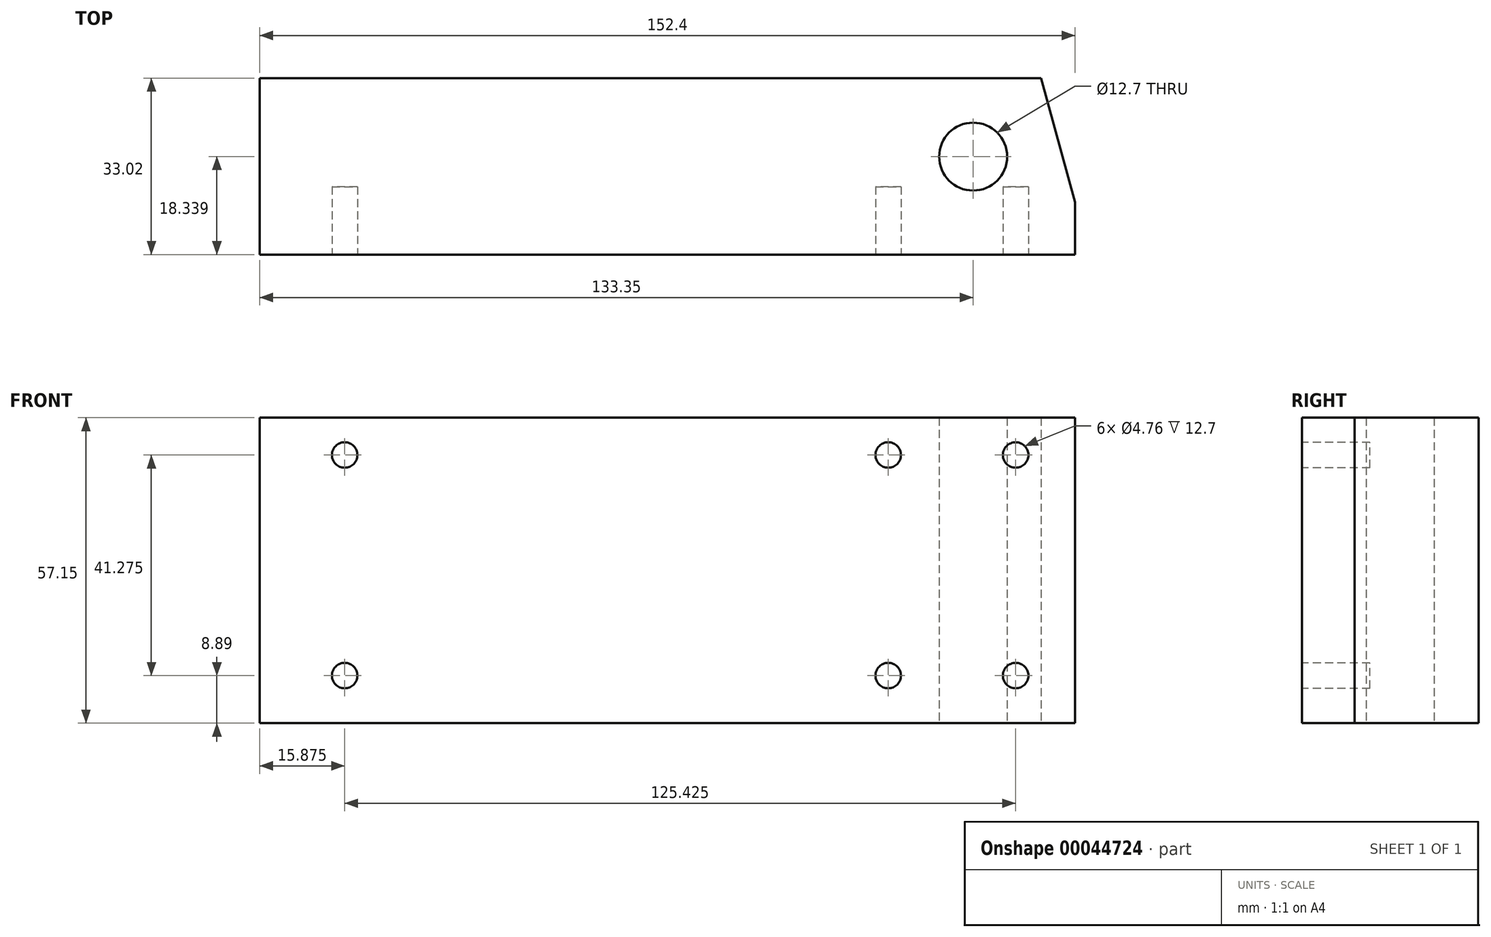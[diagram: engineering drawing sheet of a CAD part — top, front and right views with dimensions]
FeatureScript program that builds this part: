
annotation { "Feature Type Name" : "Feature", "Feature Type Description" : "" }
export const myFeature = defineFeature(function(context is Context, id is Id, definition is map)
    precondition{}
    {
        {
            var Q0;
            Q0=qCreatedBy(makeId("Top.planeOp"),FACE);
            var sketch = newSketch(context, id + "F0", { "sketchPlane" : qUnion([Q0])});
            skLineSegment(sketch, "E0", {"start": v(0, 0) * mm, "end": v(152.4, 0) * mm});
            skLineSegment(sketch, "E1", {"start": v(152.4, 0) * mm, "end": v(152.4, 33.02) * mm});
            skLineSegment(sketch, "E2", {"start": v(152.4, 33.02) * mm, "end": v(0, 33.02) * mm});
            skLineSegment(sketch, "E3", {"start": v(0, 33.02) * mm, "end": v(0, 0) * mm});
            skLineSegment(sketch, "E4", {"start": v(152.4, 18.34) * mm, "end": v(133.35, 18.34) * mm, "construction": true});
            skLineSegment(sketch, "E5", {"start": v(133.35, 18.34) * mm, "end": v(133.35, 33.02) * mm, "construction": true});
            skCircle(sketch, "E6", {"center": v(133.35, 18.34) * mm, "radius": 6.35 * mm});
            skLineSegment(sketch, "E7", {"start": v(152.4, 33.02) * mm, "end": v(146.05, 33.02) * mm, "construction": true});
            skLineSegment(sketch, "E8", {"start": v(152.4, 0) * mm, "end": v(152.4, 9.84) * mm});
            skLineSegment(sketch, "E9", {"start": v(152.4, 9.84) * mm, "end": v(146.05, 33.02) * mm});
            skSolve(sketch);
        }
        {
            var Q0;
            Q0=makeQuery(id+"F0.imprint","IMPRINT",FACE,{"disambiguationData":[TD([[makeQuery(id+"F0.imprint","IMPRINT",EDGE,{"derivedFrom":sQuery(id+"F0.wireOp",EDGE,"E0")}),1.0]])]});
            extrude(context, id + "F1", {"entities" : qUnion([Q0]), "depth" : 57.15 * mm});
        }
        {
            var Q0;
            Q0=makeQuery(id+"F1.opExtrude","SWEPT_FACE",FACE,{"disambiguationData":[OSD([sQuery(id+"F0.wireOp",EDGE,"E0")])]});
            var sketch = newSketch(context, id + "F2", { "sketchPlane" : qUnion([Q0])});
            skCircle(sketch, "E10.MirrorC", {"center": v(117.47, 50.16) * mm, "radius": 2.38 * mm});
            skCircle(sketch, "E11.MirrorC", {"center": v(117.48, 8.89) * mm, "radius": 2.38 * mm});
            skCircle(sketch, "E12.MirrorC", {"center": v(15.88, 50.16) * mm, "radius": 2.38 * mm});
            skCircle(sketch, "E13.MirrorC", {"center": v(15.88, 8.89) * mm, "radius": 2.38 * mm});
            skCircle(sketch, "E14.MirrorC", {"center": v(141.3, 8.89) * mm, "radius": 2.38 * mm});
            skCircle(sketch, "E15.MirrorC", {"center": v(141.3, 50.16) * mm, "radius": 2.38 * mm});
            skLineSegment(sketch, "E16.MirrorCS", {"start": v(117.48, 8.89) * mm, "end": v(141.3, 8.89) * mm});
            skLineSegment(sketch, "E17.MirrorCS", {"start": v(92.08, 50.16) * mm, "end": v(117.47, 50.16) * mm});
            skLineSegment(sketch, "E18.MirrorCS", {"start": v(92.08, 0) * mm, "end": v(92.08, 8.89) * mm});
            skLineSegment(sketch, "E19.MirrorCS", {"start": v(92.08, 8.89) * mm, "end": v(92.08, 50.16) * mm});
            skLineSegment(sketch, "E20.MirrorCS", {"start": v(117.47, 50.16) * mm, "end": v(117.48, 8.89) * mm});
            skLineSegment(sketch, "E21.MirrorCS", {"start": v(117.47, 50.16) * mm, "end": v(141.3, 50.16) * mm});
            skLineSegment(sketch, "E22.MirrorCS", {"start": v(141.3, 50.16) * mm, "end": v(141.3, 8.89) * mm});
            skLineSegment(sketch, "E23.MirrorCS", {"start": v(92.08, 8.89) * mm, "end": v(15.88, 8.89) * mm});
            skLineSegment(sketch, "E24.MirrorCS", {"start": v(92.08, 50.16) * mm, "end": v(15.88, 50.16) * mm});
            skLineSegment(sketch, "E25.MirrorCS", {"start": v(92.08, 8.89) * mm, "end": v(117.48, 8.89) * mm});
            skLineSegment(sketch, "E26.MirrorCS", {"start": v(15.88, 8.89) * mm, "end": v(15.88, 50.16) * mm});
            skLineSegment(sketch, "E27", {"start": v(152.4, 0) * mm, "end": v(141.3, 0) * mm, "construction": true});
            skLineSegment(sketch, "E28", {"start": v(141.3, 0) * mm, "end": v(141.3, 8.9) * mm, "construction": true});
            skSolve(sketch);
        }
        {
            var Q0;
            {var subQ1=sQuery(id+"F2.wireOp",EDGE,"E14.MirrorC");var subQ3=sQuery(id+"F2.wireOp",EDGE,"E16.MirrorCS");var subQ5=makeQuery(id+"F2.imprint","INTERSECT",VERTEX,{"derivedFrom":[subQ1,subQ3]});Q0=makeQuery(id+"F2.imprint","IMPRINT",FACE,{"disambiguationData":[TD([[makeQuery(id+"F2.imprint","IMPRINT",EDGE,{"disambiguationData":[TD([[subQ5,-1.0]])],"derivedFrom":subQ1}),1.0]])]});}
            var Q1;
            {var subQ1=sQuery(id+"F2.wireOp",EDGE,"E14.MirrorC");var subQ3=sQuery(id+"F2.wireOp",EDGE,"E16.MirrorCS");var subQ5=makeQuery(id+"F2.imprint","INTERSECT",VERTEX,{"derivedFrom":[subQ1,subQ3]});Q1=makeQuery(id+"F2.imprint","IMPRINT",FACE,{"disambiguationData":[TD([[makeQuery(id+"F2.imprint","IMPRINT",EDGE,{"disambiguationData":[TD([[subQ5,1.0]])],"derivedFrom":subQ1}),1.0]])]});}
            var Q2;
            {var subQ1=sQuery(id+"F2.wireOp",EDGE,"E15.MirrorC");var subQ3=sQuery(id+"F2.wireOp",EDGE,"E21.MirrorCS");var subQ5=makeQuery(id+"F2.imprint","INTERSECT",VERTEX,{"derivedFrom":[subQ1,subQ3]});Q2=makeQuery(id+"F2.imprint","IMPRINT",FACE,{"disambiguationData":[TD([[makeQuery(id+"F2.imprint","IMPRINT",EDGE,{"disambiguationData":[TD([[subQ5,-1.0]])],"derivedFrom":subQ1}),1.0]])]});}
            var Q3;
            {var subQ1=sQuery(id+"F2.wireOp",EDGE,"E15.MirrorC");var subQ3=sQuery(id+"F2.wireOp",EDGE,"E21.MirrorCS");var subQ5=makeQuery(id+"F2.imprint","INTERSECT",VERTEX,{"derivedFrom":[subQ1,subQ3]});Q3=makeQuery(id+"F2.imprint","IMPRINT",FACE,{"disambiguationData":[TD([[makeQuery(id+"F2.imprint","IMPRINT",EDGE,{"disambiguationData":[TD([[subQ5,1.0]])],"derivedFrom":subQ1}),1.0]])]});}
            var Q4;
            {var subQ1=sQuery(id+"F2.wireOp",EDGE,"E11.MirrorC");var subQ3=sQuery(id+"F2.wireOp",EDGE,"E16.MirrorCS");var subQ5=makeQuery(id+"F2.imprint","INTERSECT",VERTEX,{"derivedFrom":[subQ1,subQ3]});Q4=makeQuery(id+"F2.imprint","IMPRINT",FACE,{"disambiguationData":[TD([[makeQuery(id+"F2.imprint","IMPRINT",EDGE,{"disambiguationData":[TD([[subQ5,-1.0]])],"derivedFrom":subQ1}),1.0]])]});}
            var Q5;
            {var subQ1=sQuery(id+"F2.wireOp",EDGE,"E11.MirrorC");var subQ3=sQuery(id+"F2.wireOp",EDGE,"E16.MirrorCS");var subQ5=makeQuery(id+"F2.imprint","INTERSECT",VERTEX,{"derivedFrom":[subQ1,subQ3]});Q5=makeQuery(id+"F2.imprint","IMPRINT",FACE,{"disambiguationData":[TD([[makeQuery(id+"F2.imprint","IMPRINT",EDGE,{"disambiguationData":[TD([[subQ5,1.0]])],"derivedFrom":subQ1}),1.0]])]});}
            var Q6;
            {var subQ0=sQuery(id+"F2.wireOp",EDGE,"E20.MirrorCS");var subQ1=sQuery(id+"F2.wireOp",EDGE,"E10.MirrorC");var subQ2=makeQuery(id+"F2.imprint","INTERSECT",VERTEX,{"derivedFrom":[subQ1,subQ0]});Q6=makeQuery(id+"F2.imprint","IMPRINT",FACE,{"disambiguationData":[TD([[makeQuery(id+"F2.imprint","IMPRINT",EDGE,{"disambiguationData":[TD([[subQ2,1.0]])],"derivedFrom":subQ1}),1.0]])]});}
            var Q7;
            {var subQ1=sQuery(id+"F2.wireOp",EDGE,"E10.MirrorC");var subQ3=sQuery(id+"F2.wireOp",EDGE,"E17.MirrorCS");var subQ5=makeQuery(id+"F2.imprint","INTERSECT",VERTEX,{"derivedFrom":[subQ1,subQ3]});Q7=makeQuery(id+"F2.imprint","IMPRINT",FACE,{"disambiguationData":[TD([[makeQuery(id+"F2.imprint","IMPRINT",EDGE,{"disambiguationData":[TD([[subQ5,1.0]])],"derivedFrom":subQ1}),1.0]])]});}
            var Q8;
            {var subQ1=sQuery(id+"F2.wireOp",EDGE,"E10.MirrorC");var subQ3=sQuery(id+"F2.wireOp",EDGE,"E20.MirrorCS");var subQ5=makeQuery(id+"F2.imprint","INTERSECT",VERTEX,{"derivedFrom":[subQ1,subQ3]});Q8=makeQuery(id+"F2.imprint","IMPRINT",FACE,{"disambiguationData":[TD([[makeQuery(id+"F2.imprint","IMPRINT",EDGE,{"disambiguationData":[TD([[subQ5,-1.0]])],"derivedFrom":subQ1}),1.0]])]});}
            var Q9;
            {var subQ1=sQuery(id+"F2.wireOp",EDGE,"E13.MirrorC");var subQ3=sQuery(id+"F2.wireOp",EDGE,"E23.MirrorCS");var subQ5=makeQuery(id+"F2.imprint","INTERSECT",VERTEX,{"derivedFrom":[subQ1,subQ3]});Q9=makeQuery(id+"F2.imprint","IMPRINT",FACE,{"disambiguationData":[TD([[makeQuery(id+"F2.imprint","IMPRINT",EDGE,{"disambiguationData":[TD([[subQ5,-1.0]])],"derivedFrom":subQ1}),1.0]])]});}
            var Q10;
            {var subQ1=sQuery(id+"F2.wireOp",EDGE,"E13.MirrorC");var subQ3=sQuery(id+"F2.wireOp",EDGE,"E23.MirrorCS");var subQ5=makeQuery(id+"F2.imprint","INTERSECT",VERTEX,{"derivedFrom":[subQ1,subQ3]});Q10=makeQuery(id+"F2.imprint","IMPRINT",FACE,{"disambiguationData":[TD([[makeQuery(id+"F2.imprint","IMPRINT",EDGE,{"disambiguationData":[TD([[subQ5,1.0]])],"derivedFrom":subQ1}),1.0]])]});}
            var Q11;
            {var subQ0=sQuery(id+"F2.wireOp",EDGE,"E24.MirrorCS");var subQ1=sQuery(id+"F2.wireOp",EDGE,"E12.MirrorC");var subQ2=makeQuery(id+"F2.imprint","INTERSECT",VERTEX,{"derivedFrom":[subQ1,subQ0]});Q11=makeQuery(id+"F2.imprint","IMPRINT",FACE,{"disambiguationData":[TD([[makeQuery(id+"F2.imprint","IMPRINT",EDGE,{"disambiguationData":[TD([[subQ2,1.0]])],"derivedFrom":subQ1}),1.0]])]});}
            var Q12;
            {var subQ0=sQuery(id+"F2.wireOp",EDGE,"E24.MirrorCS");var subQ1=sQuery(id+"F2.wireOp",EDGE,"E12.MirrorC");var subQ2=makeQuery(id+"F2.imprint","INTERSECT",VERTEX,{"derivedFrom":[subQ1,subQ0]});Q12=makeQuery(id+"F2.imprint","IMPRINT",FACE,{"disambiguationData":[TD([[makeQuery(id+"F2.imprint","IMPRINT",EDGE,{"disambiguationData":[TD([[subQ2,-1.0]])],"derivedFrom":subQ1}),1.0]])]});}
            var Q13;
            {var subQ0=sQuery(id+"F2.wireOp",EDGE,"E25.MirrorCS");var subQ1=sQuery(id+"F2.wireOp",EDGE,"E11.MirrorC");var subQ2=makeQuery(id+"F2.imprint","INTERSECT",VERTEX,{"derivedFrom":[subQ1,subQ0]});Q13=makeQuery(id+"F2.imprint","IMPRINT",FACE,{"disambiguationData":[TD([[makeQuery(id+"F2.imprint","IMPRINT",EDGE,{"disambiguationData":[TD([[subQ2,1.0]])],"derivedFrom":subQ1}),1.0]])]});}
            var Q14;
            Q14=sQuery(id+"F2.wireOp",EDGE,"E15.MirrorC");
            var Q15;
            Q15=sQuery(id+"F2.wireOp",EDGE,"E14.MirrorC");
            var Q16;
            Q16=sQuery(id+"F2.wireOp",EDGE,"E11.MirrorC");
            var Q17;
            Q17=sQuery(id+"F2.wireOp",EDGE,"E10.MirrorC");
            var Q18;
            Q18=sQuery(id+"F2.wireOp",EDGE,"E13.MirrorC");
            var Q19;
            Q19=sQuery(id+"F2.wireOp",EDGE,"E12.MirrorC");
            extrude(context, id + "F3", {"entities" : qUnion([Q0, Q1, Q2, Q3, Q4, Q5, Q6, Q7, Q8, Q9, Q10, Q11, Q12, Q13]), "operationType" : NewBodyOperationType.REMOVE, "surfaceEntities" : qUnion([Q14, Q15, Q16, Q17, Q18, Q19]), "oppositeDirection" : true, "depth" : 12.7 * mm});
        }
    });
